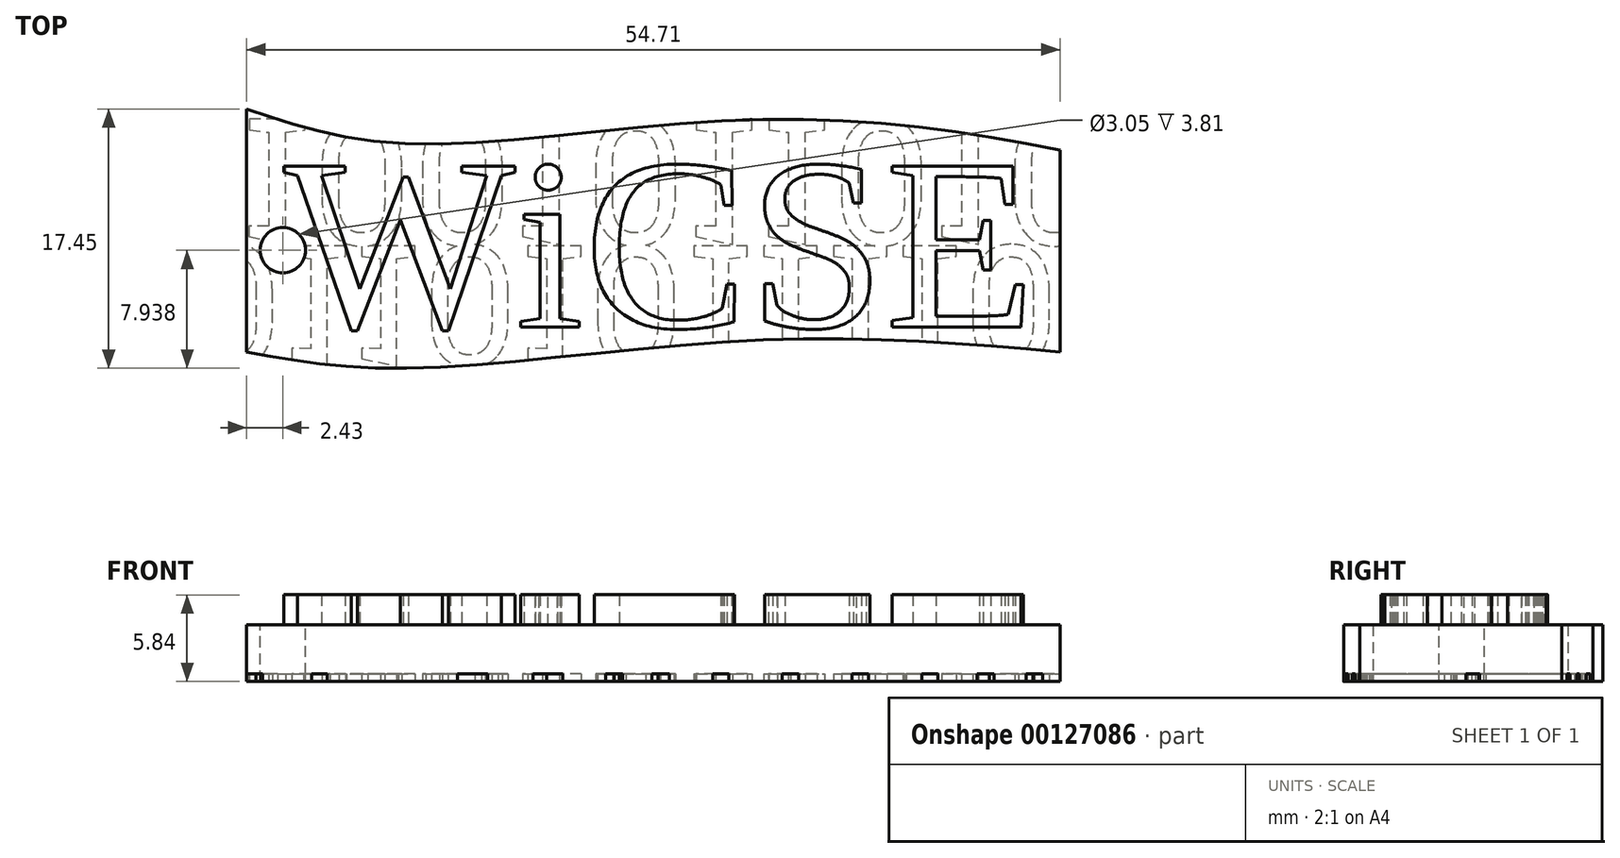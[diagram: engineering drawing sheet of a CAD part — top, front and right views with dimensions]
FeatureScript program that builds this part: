
annotation { "Feature Type Name" : "Feature", "Feature Type Description" : "" }
export const myFeature = defineFeature(function(context is Context, id is Id, definition is map)
    precondition{}
    {
        {
            var Q0;
            Q0=qCreatedBy(makeId("Top.planeOp"),FACE);
            var sketch = newSketch(context, id + "F0", { "sketchPlane" : qUnion([Q0])});
            skLineSegment(sketch, "E0.bottom", {"start": v(-2.47, 14.68) * mm, "end": v(52.24, 14.68) * mm, "construction": true});
            skLineSegment(sketch, "E0.top", {"start": v(-2.47, -1.67) * mm, "end": v(52.24, -1.67) * mm, "construction": true});
            skLineSegment(sketch, "E0.left", {"start": v(-2.47, 14.68) * mm, "end": v(-2.47, -1.67) * mm});
            skLineSegment(sketch, "E0.right", {"start": v(52.24, 14.68) * mm, "end": v(52.24, -1.67) * mm});
            skLineSegment(sketch, "E1", {"start": v(8.11, 14.68) * mm, "end": v(8.11, -1.67) * mm, "construction": true});
            skLineSegment(sketch, "E2", {"start": v(31.55, 14.68) * mm, "end": v(31.55, -1.67) * mm, "construction": true});
            skFitSpline(sketch, "E3", {"points": [v(-2.47, 14.68) * mm, v(8.11, 12.34) * mm, v(31.55, 13.96) * mm, v(52.24, 11.92) * mm], "startDerivative": vector(35.08, -11.82) * mm, "endDerivative": vector(51.59, -10.31) * mm});
            skLineSegment(sketch, "E4", {"start": v(8.11, -1.67) * mm, "end": v(8.11, -5.82) * mm, "construction": true});
            skLineSegment(sketch, "E5", {"start": v(31.55, -1.67) * mm, "end": v(31.55, -5.06) * mm, "construction": true});
            skFitSpline(sketch, "E6", {"points": [v(-2.47, -1.67) * mm, v(8.11, -2.77) * mm, v(31.55, -0.9) * mm, v(52.24, -1.67) * mm], "startDerivative": vector(35.9, -6.9) * mm, "endDerivative": vector(51.8, -4.76) * mm});
            skSolve(sketch);
        }
        {
            var Q0;
            Q0 = qSketchRegion(id + "F0", true);
            extrude(context, id + "F1", {"entities" : qUnion([Q0]), "depth" : 3.8 * mm});
        }
        {
            var Q0;
            Q0=makeQuery(id+"F1.opExtrude","CAP_FACE",FACE,{"disambiguationData":[OSD([sQuery(id+"F0.wireOp",EDGE,"E0.left"),sQuery(id+"F0.wireOp",EDGE,"E0.right"),sQuery(id+"F0.wireOp",EDGE,"E3"),sQuery(id+"F0.wireOp",EDGE,"E6")])],"isStart":false});
            var sketch = newSketch(context, id + "F2", { "sketchPlane" : qUnion([Q0])});
            skText(sketch, "E7", { "text": "WiCSE", "fontName": "Tinos-Regular.ttf"});
            const initialGuessF2  = {"E7": [0, 0, 1, 0, 0.01192]};
            skSetInitialGuess(sketch, initialGuessF2);
            skSolve(sketch);
        }
        {
            var Q0;
            Q0 = qSketchRegion(id + "F2", true);
            extrude(context, id + "F3", {"entities" : qUnion([Q0]), "depth" : 2.03 * mm});
        }
        {
            var Q0;
            Q0=makeQuery(id+"F1.opExtrude","CAP_FACE",FACE,{"disambiguationData":[OSD([sQuery(id+"F0.wireOp",EDGE,"E0.left"),sQuery(id+"F0.wireOp",EDGE,"E0.right"),sQuery(id+"F0.wireOp",EDGE,"E3"),sQuery(id+"F0.wireOp",EDGE,"E6")])],"isStart":true});
            var sketch = newSketch(context, id + "F4", { "sketchPlane" : qUnion([Q0])});
            skText(sketch, "E8", { "text": "1001011010", "fontName": "RobotoSlab-Regular.ttf"});
            const initialGuessF4  = {"E8": [-0.003, -0.01399, 1, 0, 0.00854]};
            skSetInitialGuess(sketch, initialGuessF4);
            skSolve(sketch);
        }
        {
            var Q0;
            Q0 = qSketchRegion(id + "F4", true);
            extrude(context, id + "F5", {"entities" : qUnion([Q0]), "operationType" : NewBodyOperationType.REMOVE, "oppositeDirection" : true, "depth" : 0.5 * mm});
        }
        {
            var Q0;
            {var subQ0=sQuery(id+"F0.wireOp",EDGE,"E0.left");var subQ1=sQuery(id+"F0.wireOp",EDGE,"E6");var subQ2=sQuery(id+"F0.wireOp",EDGE,"E3");var subQ3=sQuery(id+"F0.wireOp",EDGE,"E0.right");Q0=makeQuery(id+"F5.boolean.opBoolean","SPLIT",FACE,{"disambiguationData":[TD([makeQuery(id+"F1.opExtrude","SWEPT_FACE",FACE,{"disambiguationData":[OSD([subQ0])]})])],"derivedFrom":makeQuery(id+"F1.opExtrude","CAP_FACE",FACE,{"disambiguationData":[OSD([subQ0,subQ3,subQ2,subQ1])],"isStart":true})});}
            var sketch = newSketch(context, id + "F6", { "sketchPlane" : qUnion([Q0])});
            skText(sketch, "E9", { "text": "011010111101", "fontName": "RobotoSlab-Regular.ttf"});
            const initialGuessF6  = {"E9": [-0.00657, -0.00546, 1, 0, 0.00819]};
            skSetInitialGuess(sketch, initialGuessF6);
            skSolve(sketch);
        }
        {
            var Q0;
            Q0 = qSketchRegion(id + "F6", true);
            extrude(context, id + "F7", {"entities" : qUnion([Q0]), "operationType" : NewBodyOperationType.REMOVE, "oppositeDirection" : true, "depth" : 0.5 * mm});
        }
        {
            var Q0;
            Q0=makeQuery(id+"F1.opExtrude","CAP_FACE",FACE,{"disambiguationData":[OSD([sQuery(id+"F0.wireOp",EDGE,"E0.left"),sQuery(id+"F0.wireOp",EDGE,"E0.right"),sQuery(id+"F0.wireOp",EDGE,"E3"),sQuery(id+"F0.wireOp",EDGE,"E6")])],"isStart":false});
            var sketch = newSketch(context, id + "F8", { "sketchPlane" : qUnion([Q0])});
            skCircle(sketch, "E10", {"center": v(-0.04, 5.17) * mm, "radius": 1.52 * mm});
            skSolve(sketch);
        }
        {
            var Q0;
            Q0 = qSketchRegion(id + "F8", true);
            var Q1;
            Q1=sQuery(id+"F8.wireOp",EDGE,"E10");
            var Q2;
            {var subQ6=sQuery(id+"F0.wireOp",EDGE,"E3");var subQ10=sQuery(id+"F0.wireOp",EDGE,"E0.left");var subQ11=makeQuery(id+"F1.opExtrude","SWEPT_FACE",FACE,{"disambiguationData":[OSD([subQ10])]});var subQ17=sQuery(id+"F0.wireOp",EDGE,"E6");var subQ21=makeQuery(id+"F5.opExtrude","SWEPT_FACE",FACE,{"disambiguationData":[OSD([sQuery(id+"F4.wireOp",EDGE,"E8.sketch_text.stroke-0")])]});var subQ28=sQuery(id+"F0.wireOp",EDGE,"E0.right");Q2=makeQuery(id+"F7.boolean.opBoolean","SPLIT",FACE,{"disambiguationData":[TD([makeQuery(id+"F5.boolean.opBoolean","COPY",FACE,{"derivedFrom":subQ21})])],"derivedFrom":makeQuery(id+"F5.boolean.opBoolean","SPLIT",FACE,{"disambiguationData":[TD([subQ11])],"derivedFrom":makeQuery(id+"F1.opExtrude","CAP_FACE",FACE,{"disambiguationData":[OSD([subQ10,subQ28,subQ6,subQ17])],"isStart":true})})});}
            extrude(context, id + "F9", {"entities" : qUnion([Q0]), "operationType" : NewBodyOperationType.REMOVE, "surfaceEntities" : qUnion([Q1]), "oppositeDirection" : true, "endBoundEntityFace" : qUnion([Q2]), "depth" : 12.7 * mm});
        }
    });
